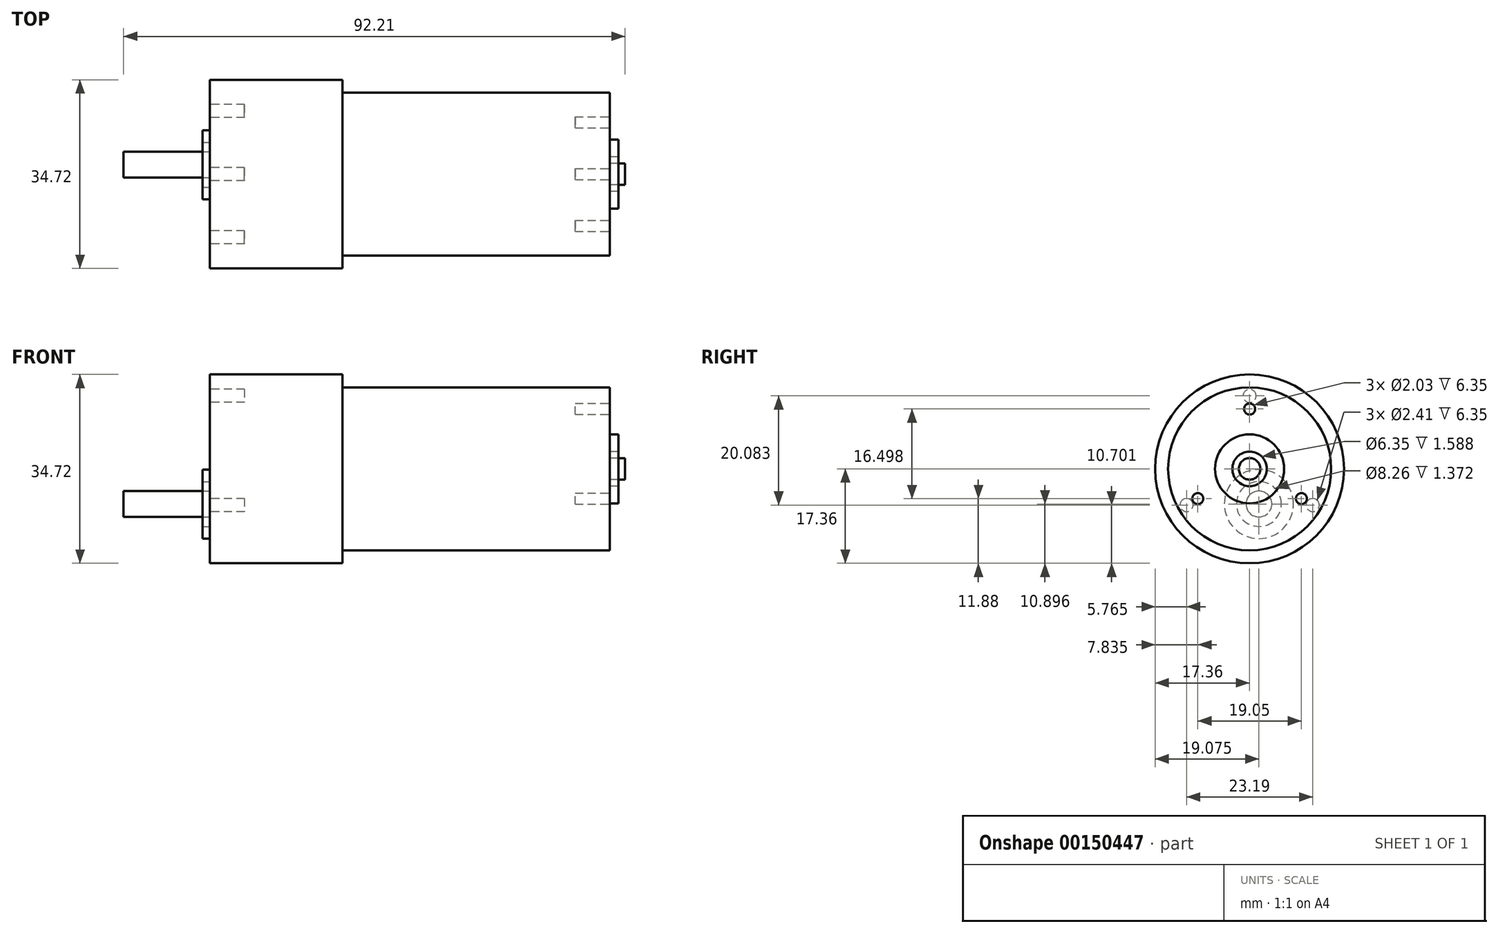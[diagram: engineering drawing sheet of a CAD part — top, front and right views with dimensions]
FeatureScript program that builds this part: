
annotation { "Feature Type Name" : "Feature", "Feature Type Description" : "" }
export const myFeature = defineFeature(function(context is Context, id is Id, definition is map)
    precondition{}
    {
        {
            var Q0;
            Q0=qCreatedBy(makeId("Right.planeOp"),FACE);
            var sketch = newSketch(context, id + "F0", { "sketchPlane" : qUnion([Q0])});
            skCircle(sketch, "E0", {"center": v(0, 0) * mm, "radius": 17.36 * mm});
            skSolve(sketch);
        }
        {
            var Q0;
            Q0=makeQuery(id+"F0.imprint","IMPRINT",FACE,{"disambiguationData":[TD([[makeQuery(id+"F0.imprint","IMPRINT",EDGE,{"derivedFrom":sQuery(id+"F0.wireOp",EDGE,"E0")}),1.0]])]});
            extrude(context, id + "F1", {"entities" : qUnion([Q0]), "depth" : 24.38 * mm});
        }
        {
            var Q0;
            Q0=makeQuery(id+"F1.opExtrude","CAP_FACE",FACE,{"disambiguationData":[OSD([sQuery(id+"F0.wireOp",EDGE,"E0")])],"isStart":false});
            var sketch = newSketch(context, id + "F2", { "sketchPlane" : qUnion([Q0])});
            skCircle(sketch, "E1", {"center": v(0, 0) * mm, "radius": 14.99 * mm});
            skSolve(sketch);
        }
        {
            var Q0;
            Q0 = qSketchRegion(id + "F2", true);
            extrude(context, id + "F3", {"entities" : qUnion([Q0]), "operationType" : NewBodyOperationType.ADD, "depth" : 49.1 * mm});
        }
        {
            var Q0;
            Q0=makeQuery(id+"F3.opExtrude","CAP_FACE",FACE,{"disambiguationData":[OSD([sQuery(id+"F2.wireOp",EDGE,"E1")])],"isStart":false});
            var sketch = newSketch(context, id + "F4", { "sketchPlane" : qUnion([Q0])});
            skCircle(sketch, "E2", {"center": v(0, 11.02) * mm, "radius": 1.02 * mm});
            skCircle(sketch, "E3", {"center": v(9.52, -5.48) * mm, "radius": 1.02 * mm});
            skCircle(sketch, "E4", {"center": v(-9.53, -5.48) * mm, "radius": 1.02 * mm});
            skLineSegment(sketch, "E5", {"start": v(0, 11.02) * mm, "end": v(0, 14.99) * mm, "construction": true});
            skLineSegment(sketch, "E6", {"start": v(9.52, -5.48) * mm, "end": v(12.99, -7.47) * mm, "construction": true});
            skLineSegment(sketch, "E7", {"start": v(-12.99, -7.47) * mm, "end": v(-9.53, -5.48) * mm, "construction": true});
            skSolve(sketch);
        }
        {
            var Q0;
            Q0 = qSketchRegion(id + "F4", true);
            extrude(context, id + "F5", {"entities" : qUnion([Q0]), "operationType" : NewBodyOperationType.REMOVE, "oppositeDirection" : true, "depth" : 6.35 * mm});
        }
        {
            var Q0;
            Q0=makeQuery(id+"F3.opExtrude","CAP_FACE",FACE,{"disambiguationData":[OSD([sQuery(id+"F2.wireOp",EDGE,"E1")])],"isStart":false});
            var sketch = newSketch(context, id + "F6", { "sketchPlane" : qUnion([Q0])});
            skCircle(sketch, "E8", {"center": v(0, 0) * mm, "radius": 3.18 * mm});
            skCircle(sketch, "E9", {"center": v(0, 0) * mm, "radius": 6.35 * mm});
            skSolve(sketch);
        }
        {
            var Q0;
            Q0 = qSketchRegion(id + "F6", true);
            extrude(context, id + "F7", {"entities" : qUnion([Q0]), "operationType" : NewBodyOperationType.ADD, "depth" : 1.59 * mm});
        }
        {
            var Q0;
            Q0=makeQuery(id+"F7.boolean.opBoolean","SPLIT",FACE,{"disambiguationData":[TD([makeQuery(id+"F7.opExtrude","SWEPT_FACE",FACE,{"disambiguationData":[OSD([sQuery(id+"F6.wireOp",EDGE,"E8")])]})])],"derivedFrom":makeQuery(id+"F3.opExtrude","CAP_FACE",FACE,{"disambiguationData":[OSD([sQuery(id+"F2.wireOp",EDGE,"E1")])],"isStart":false})});
            var sketch = newSketch(context, id + "F8", { "sketchPlane" : qUnion([Q0])});
            skCircle(sketch, "E10", {"center": v(0, 0) * mm, "radius": 1.98 * mm});
            skSolve(sketch);
        }
        {
            var Q0;
            Q0 = qSketchRegion(id + "F8", true);
            extrude(context, id + "F9", {"entities" : qUnion([Q0]), "operationType" : NewBodyOperationType.ADD, "depth" : 2.84 * mm});
        }
        {
            var Q0;
            Q0=makeQuery(id+"F1.opExtrude","CAP_FACE",FACE,{"disambiguationData":[OSD([sQuery(id+"F0.wireOp",EDGE,"E0")])],"isStart":true});
            var sketch = newSketch(context, id + "F10", { "sketchPlane" : qUnion([Q0])});
            skCircle(sketch, "E11", {"center": v(0, 13.42) * mm, "radius": 1.2 * mm});
            skCircle(sketch, "E12", {"center": v(11.6, -6.66) * mm, "radius": 1.2 * mm});
            skCircle(sketch, "E13", {"center": v(-11.6, -6.66) * mm, "radius": 1.2 * mm});
            skSolve(sketch);
        }
        {
            var Q0;
            Q0 = qSketchRegion(id + "F10", true);
            extrude(context, id + "F11", {"entities" : qUnion([Q0]), "operationType" : NewBodyOperationType.REMOVE, "oppositeDirection" : true, "depth" : 6.35 * mm});
        }
        {
            var Q0;
            Q0=makeQuery(id+"F1.opExtrude","CAP_FACE",FACE,{"disambiguationData":[OSD([sQuery(id+"F0.wireOp",EDGE,"E0")])],"isStart":true});
            var sketch = newSketch(context, id + "F12", { "sketchPlane" : qUnion([Q0])});
            skCircle(sketch, "E14", {"center": v(-1.71, -6.46) * mm, "radius": 6.35 * mm});
            skCircle(sketch, "E15", {"center": v(-1.71, -6.46) * mm, "radius": 4.13 * mm});
            skLineSegment(sketch, "E16", {"start": v(-1.71, -12.81) * mm, "end": v(20.09, -12.81) * mm, "construction": true});
            skLineSegment(sketch, "E17", {"start": v(0, 13.42) * mm, "end": v(19.94, 13.42) * mm, "construction": true});
            skLineSegment(sketch, "E18", {"start": v(11.6, -6.66) * mm, "end": v(11.6, -0.39) * mm, "construction": true});
            skLineSegment(sketch, "E19", {"start": v(-8.06, -6.46) * mm, "end": v(-8.06, 3.42) * mm, "construction": true});
            skSolve(sketch);
        }
        {
            var Q0;
            Q0 = qSketchRegion(id + "F12", true);
            extrude(context, id + "F13", {"entities" : qUnion([Q0]), "operationType" : NewBodyOperationType.ADD, "depth" : 1.37 * mm});
        }
        {
            var Q0;
            Q0=makeQuery(id+"F13.boolean.opBoolean","SPLIT",FACE,{"disambiguationData":[TD([makeQuery(id+"F13.opExtrude","SWEPT_FACE",FACE,{"disambiguationData":[OSD([sQuery(id+"F12.wireOp",EDGE,"E15")])]})])],"derivedFrom":makeQuery(id+"F1.opExtrude","CAP_FACE",FACE,{"disambiguationData":[OSD([sQuery(id+"F0.wireOp",EDGE,"E0")])],"isStart":true})});
            var sketch = newSketch(context, id + "F14", { "sketchPlane" : qUnion([Q0])});
            skCircle(sketch, "E20", {"center": v(-1.71, -6.46) * mm, "radius": 2.38 * mm});
            skSolve(sketch);
        }
        {
            var Q0;
            Q0 = qSketchRegion(id + "F14", true);
            extrude(context, id + "F15", {"entities" : qUnion([Q0]), "operationType" : NewBodyOperationType.ADD, "depth" : 15.88 * mm});
        }
    });
